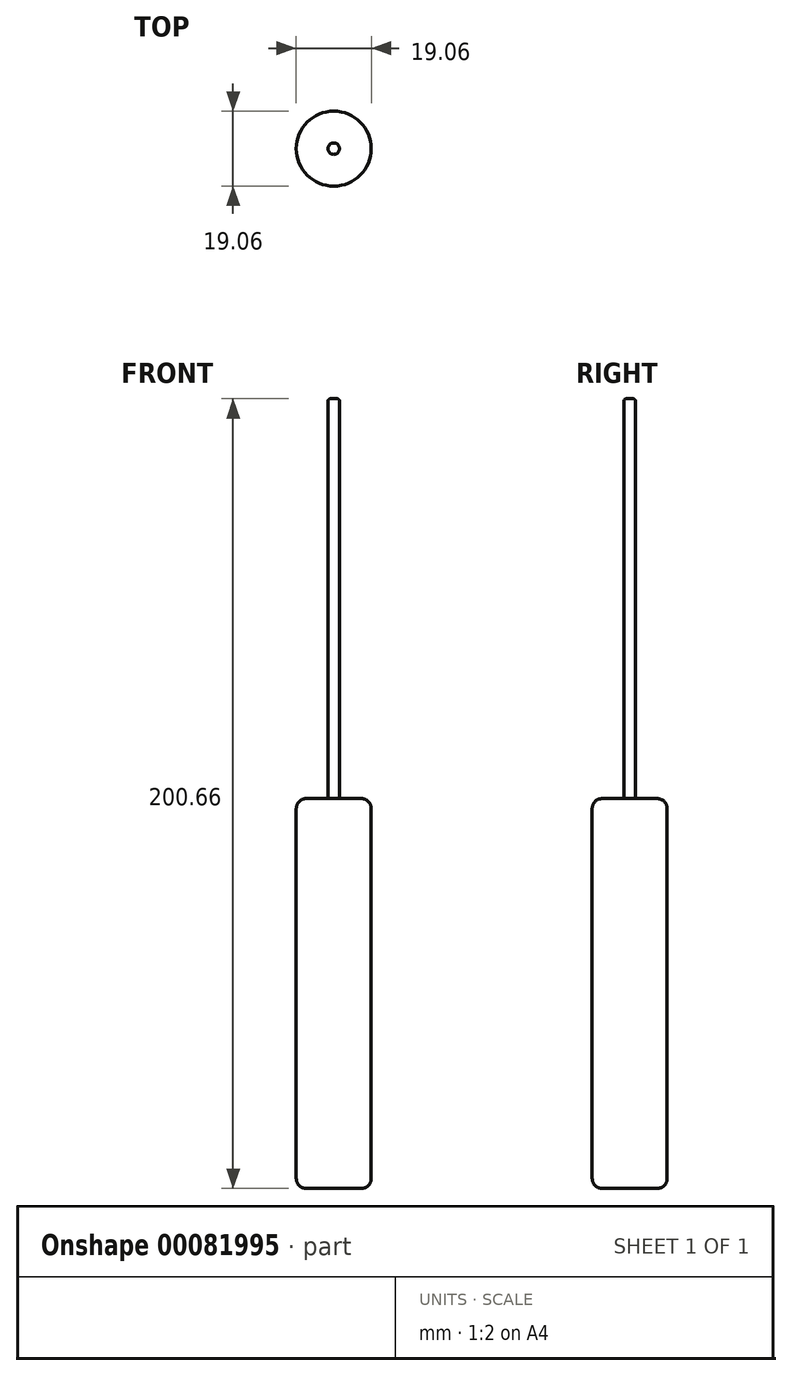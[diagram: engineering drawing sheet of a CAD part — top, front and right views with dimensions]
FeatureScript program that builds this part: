
annotation { "Feature Type Name" : "Feature", "Feature Type Description" : "" }
export const myFeature = defineFeature(function(context is Context, id is Id, definition is map)
    precondition{}
    {
        {
            var Q0;
            Q0=qCreatedBy(makeId("Top.planeOp"),FACE);
            var sketch = newSketch(context, id + "F0", { "sketchPlane" : qUnion([Q0])});
            skCircle(sketch, "E0", {"center": v(0, 0) * mm, "radius": 9.53 * mm});
            skSolve(sketch);
        }
        {
            var Q0;
            Q0 = qSketchRegion(id + "F0", true);
            extrude(context, id + "F1", {"entities" : qUnion([Q0]), "depth" : 99.06 * mm});
        }
        {
            var Q0;
            Q0=makeQuery(id+"F1.opExtrude","CAP_FACE",FACE,{"disambiguationData":[OSD([sQuery(id+"F0.wireOp",EDGE,"E0")])],"isStart":false});
            var sketch = newSketch(context, id + "F2", { "sketchPlane" : qUnion([Q0])});
            skCircle(sketch, "E1", {"center": v(0, 0) * mm, "radius": 1.46 * mm});
            skSolve(sketch);
        }
        {
            var Q0;
            Q0 = qSketchRegion(id + "F2", true);
            extrude(context, id + "F3", {"entities" : qUnion([Q0]), "operationType" : NewBodyOperationType.ADD, "depth" : 101.6 * mm});
        }
        {
            var Q0;
            Q0=makeQuery(id+"F3.opExtrude","CAP_EDGE",EDGE,{"disambiguationData":[OSD([sQuery(id+"F2.wireOp",EDGE,"E1")])],"isStart":false});
            fillet(context, id + "F4", {"entities" : qUnion([Q0]), "radius" : 0.64 * mm, "tangentPropagation" : true, "allowEdgeOverflow" : false});
        }
        {
            var Q0;
            Q0=makeQuery(id+"F1.opExtrude","CAP_EDGE",EDGE,{"disambiguationData":[OSD([sQuery(id+"F0.wireOp",EDGE,"E0")])],"isStart":true});
            fillet(context, id + "F5", {"entities" : qUnion([Q0]), "radius" : 2.54 * mm, "tangentPropagation" : true, "allowEdgeOverflow" : false});
        }
        {
            var Q0;
            Q0=makeQuery(id+"F1.opExtrude","CAP_EDGE",EDGE,{"disambiguationData":[OSD([sQuery(id+"F0.wireOp",EDGE,"E0")])],"isStart":false});
            fillet(context, id + "F6", {"entities" : qUnion([Q0]), "radius" : 2.54 * mm, "tangentPropagation" : true, "allowEdgeOverflow" : false});
        }
    });
